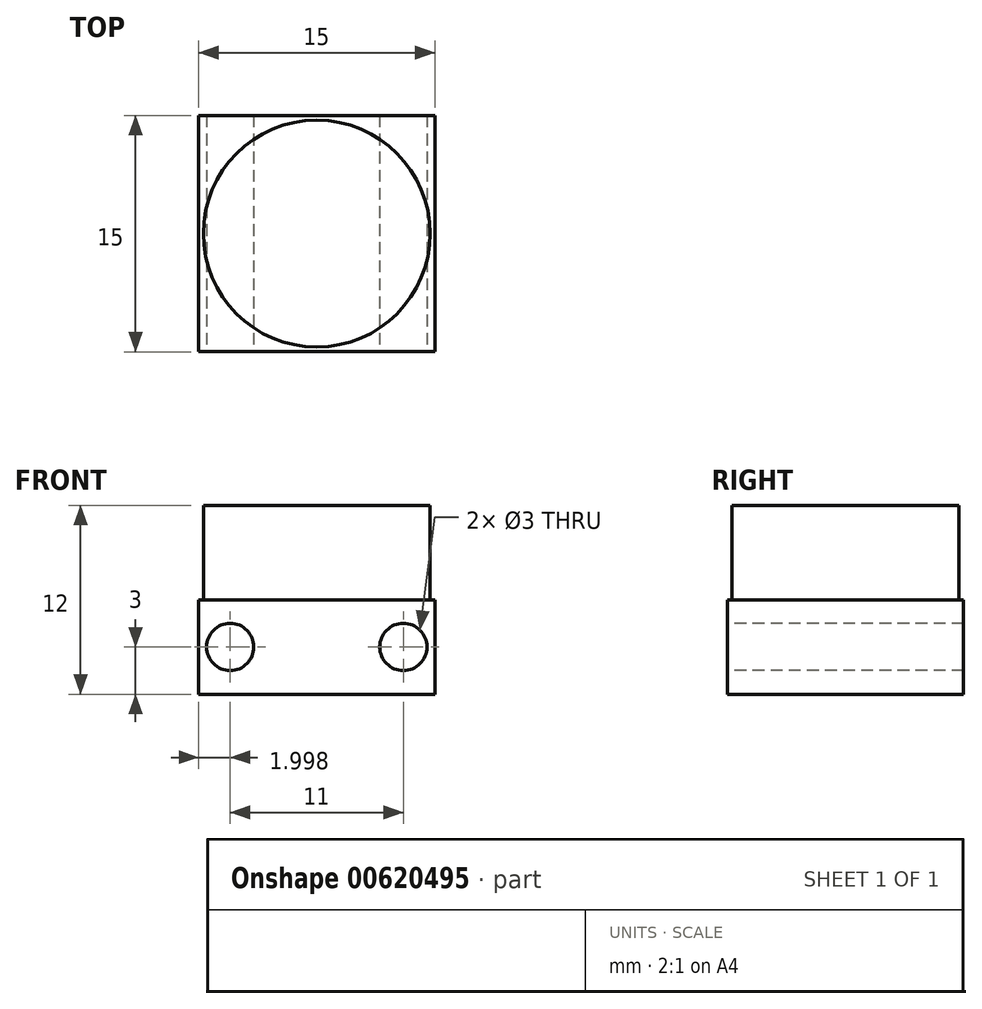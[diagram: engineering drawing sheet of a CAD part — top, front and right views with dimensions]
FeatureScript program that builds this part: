
annotation { "Feature Type Name" : "Feature", "Feature Type Description" : "" }
export const myFeature = defineFeature(function(context is Context, id is Id, definition is map)
    precondition{}
    {
        {
            var Q0;
            Q0=qCreatedBy(makeId("Top.planeOp"),FACE);
            var sketch = newSketch(context, id + "F0", { "sketchPlane" : qUnion([Q0])});
            skLineSegment(sketch, "E0.bottom", {"start": v(-8.25, 9.01) * mm, "end": v(6.75, 9.01) * mm});
            skLineSegment(sketch, "E0.top", {"start": v(-8.25, -5.99) * mm, "end": v(6.75, -5.99) * mm});
            skLineSegment(sketch, "E0.left", {"start": v(-8.25, 9.01) * mm, "end": v(-8.25, -5.99) * mm});
            skLineSegment(sketch, "E0.right", {"start": v(6.75, 9.01) * mm, "end": v(6.75, -5.99) * mm});
            skSolve(sketch);
        }
        {
            var Q0;
            Q0=makeQuery(id+"F0.imprint","IMPRINT",FACE,{"disambiguationData":[TD([[makeQuery(id+"F0.imprint","IMPRINT",EDGE,{"derivedFrom":sQuery(id+"F0.wireOp",EDGE,"E0.bottom")}),-1.0]])]});
            extrude(context, id + "F1", {"entities" : qUnion([Q0]), "depth" : 6 * mm, "offsetDistance" : 25.4 * mm});
        }
        {
            var Q0;
            Q0=makeQuery(id+"F1.opExtrude","SWEPT_FACE",FACE,{"disambiguationData":[OSD([sQuery(id+"F0.wireOp",EDGE,"E0.top")])]});
            var sketch = newSketch(context, id + "F2", { "sketchPlane" : qUnion([Q0])});
            skCircle(sketch, "E1", {"center": v(-6.25, 3) * mm, "radius": 1.5 * mm});
            skPoint(sketch, "E1.centerSnap0", {"position": v(-8.25, 3) * mm});
            skSolve(sketch);
        }
        {
            var Q0;
            Q0=makeQuery(id+"F2.imprint","IMPRINT",FACE,{"disambiguationData":[TD([[makeQuery(id+"F2.imprint","IMPRINT",EDGE,{"derivedFrom":sQuery(id+"F2.wireOp",EDGE,"E1")}),1.0]])]});
            extrude(context, id + "F3", {"entities" : qUnion([Q0]), "operationType" : NewBodyOperationType.REMOVE, "oppositeDirection" : true, "depth" : 15 * mm, "offsetDistance" : 25.4 * mm});
        }
        {
            var Q0;
            Q0=makeQuery(id+"F1.opExtrude","SWEPT_FACE",FACE,{"disambiguationData":[OSD([sQuery(id+"F0.wireOp",EDGE,"E0.top")])]});
            var sketch = newSketch(context, id + "F4", { "sketchPlane" : qUnion([Q0])});
            skCircle(sketch, "E2", {"center": v(4.75, 3) * mm, "radius": 1.5 * mm});
            skPoint(sketch, "E2.centerSnap0", {"position": v(6.75, 3) * mm});
            skSolve(sketch);
        }
        {
            var Q0;
            Q0=makeQuery(id+"F4.imprint","IMPRINT",FACE,{"disambiguationData":[TD([[makeQuery(id+"F4.imprint","IMPRINT",EDGE,{"derivedFrom":sQuery(id+"F4.wireOp",EDGE,"E2")}),1.0]])]});
            extrude(context, id + "F5", {"entities" : qUnion([Q0]), "operationType" : NewBodyOperationType.REMOVE, "oppositeDirection" : true, "depth" : 15 * mm, "offsetDistance" : 25.4 * mm});
        }
        {
            var Q0;
            Q0=makeQuery(id+"F1.opExtrude","CAP_FACE",FACE,{"disambiguationData":[OSD([sQuery(id+"F0.wireOp",EDGE,"E0.bottom"),sQuery(id+"F0.wireOp",EDGE,"E0.top"),sQuery(id+"F0.wireOp",EDGE,"E0.left"),sQuery(id+"F0.wireOp",EDGE,"E0.right")])],"isStart":false});
            var sketch = newSketch(context, id + "F6", { "sketchPlane" : qUnion([Q0])});
            skCircle(sketch, "E3", {"center": v(-0.75, 1.51) * mm, "radius": 7.2 * mm});
            skPoint(sketch, "E3.centerSnap0", {"position": v(-0.75, 9.01) * mm});
            skPoint(sketch, "E3.centerSnap1", {"position": v(-8.25, 1.51) * mm});
            skSolve(sketch);
        }
        {
            var Q0;
            Q0=makeQuery(id+"F6.imprint","IMPRINT",FACE,{"disambiguationData":[TD([[makeQuery(id+"F6.imprint","IMPRINT",EDGE,{"derivedFrom":sQuery(id+"F6.wireOp",EDGE,"E3")}),1.0]])]});
            extrude(context, id + "F7", {"entities" : qUnion([Q0]), "operationType" : NewBodyOperationType.ADD, "depth" : 6 * mm, "offsetDistance" : 25.4 * mm});
        }
    });
